# Revit family: SB-3
name_source: partatom
category: Modelos genéricos
units: mm (PartAtom-declared; Revit-internal decimal feet)

## family parameters
Compartido = No
Corte con vacíos al cargar = No
Cota de conector redondo = Diámetro de uso
Puede alojar armadura = No
Punto de cálculo de habitación = No
Se basa en plano de trabajo = No
Siempre vertical = Sí
Tipo de pieza = Normal

## types (6) — shared parameters
Fabricante = Casals ventilación
e = 1 mm  [stored 0.00328084 ft]

## per-type parameters (varying)
| type | A | B | C | D1 | D2 | H2 | Modelo | URL | ØMOTOR |
| sb-3 3015 | 310 mm  [stored 1.01706 ft] | 180 mm  [stored 0.590551 ft] | 330 mm | 300 mm | 150 mm | 180 mm  [stored 0.590551 ft] | SB-3 3015 EEC | https://www.casals.com | 95 mm |
| SB-3 4020 | 410 mm  [stored 1.34514 ft] | 230 mm  [stored 0.754593 ft] | 430 mm | 400 mm  [stored 1.31234 ft] | 200 mm  [stored 0.656168 ft] | 244 mm | SB-3 4020 EEC | https://www.casals.com
https://www.casals.com
https://www.casals.com | 95 mm |
| SB-3 5035 | 510 mm  [stored 1.67323 ft] | 383 mm  [stored 1.25656 ft] | 530 mm  [stored 1.73885 ft] | 500 mm  [stored 1.64042 ft] | 353 mm  [stored 1.15814 ft] | 387 mm | SB-3 5035 EEC | https://www.casals.com
https://www.casals.com
https://www.casals.com | 115 mm  [stored 0.377297 ft] |
| SB-3 6040 | 610 mm  [stored 2.00131 ft] | 430 mm | 630 mm  [stored 2.06693 ft] | 600 mm | 400 mm  [stored 1.31234 ft] | 447 mm | SB-3 6040 EEC | https://www.casals.com | 115 mm  [stored 0.377297 ft] |
| SB-3 7050 | 710 mm | 530 mm  [stored 1.73885 ft] | 730 mm  [stored 2.39501 ft] | 700 mm  [stored 2.29659 ft] | 500 mm  [stored 1.64042 ft] | 560 mm  [stored 1.83727 ft] | SB-3 7050 EEC | https://www.casals.com | 163 mm  [stored 0.534777 ft] |
| SB-3 8060 | 910 mm | 631 mm  [stored 2.07021 ft] | 830 mm  [stored 2.7231 ft] | 800 mm  [stored 2.62467 ft] | 601 mm  [stored 1.97178 ft] | 661 mm  [stored 2.16864 ft] | SB-3 8060 EEC | https://www.casals.com
https://www.casals.com | 163 mm  [stored 0.534777 ft] |

note: [stored X ft] marks values corroborated as IEEE doubles in the binary element streams (Revit-internal decimal feet)
